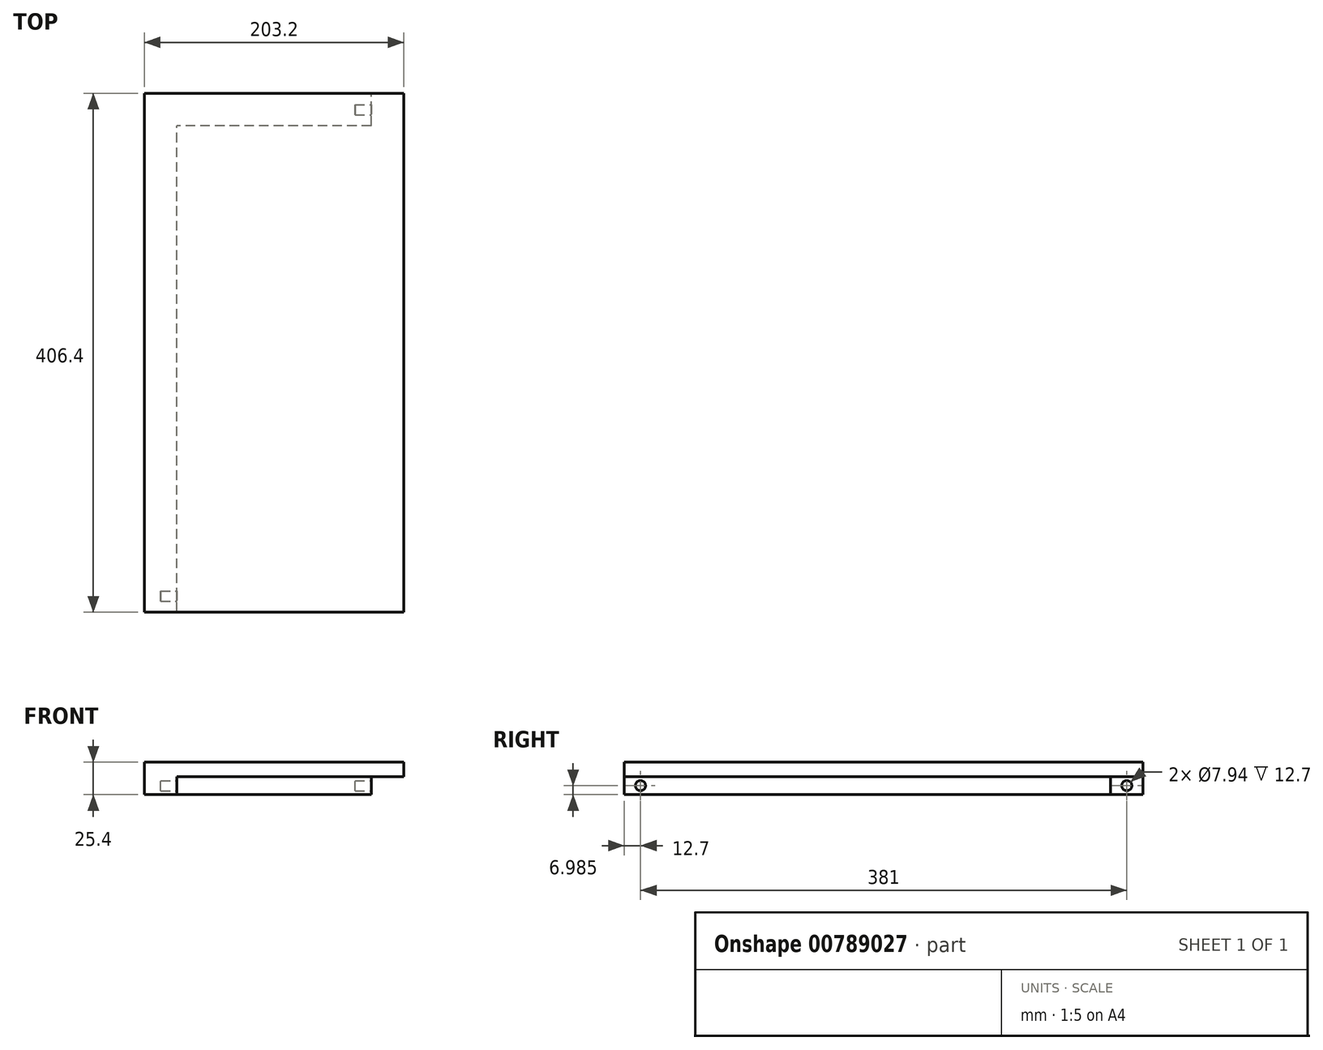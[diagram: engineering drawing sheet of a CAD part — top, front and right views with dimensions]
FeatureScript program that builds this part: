
annotation { "Feature Type Name" : "Feature", "Feature Type Description" : "" }
export const myFeature = defineFeature(function(context is Context, id is Id, definition is map)
    precondition{}
    {
        {
            var Q0;
            Q0=qCreatedBy(makeId("Top.planeOp"),FACE);
            var sketch = newSketch(context, id + "F0", { "sketchPlane" : qUnion([Q0])});
            skLineSegment(sketch, "E0.bottom", {"start": v(101.6, 203.2) * mm, "end": v(-101.6, 203.2) * mm});
            skLineSegment(sketch, "E0.top", {"start": v(101.6, -203.2) * mm, "end": v(-101.6, -203.2) * mm});
            skLineSegment(sketch, "E0.left", {"start": v(101.6, 203.2) * mm, "end": v(101.6, -203.2) * mm});
            skLineSegment(sketch, "E0.right", {"start": v(-101.6, 203.2) * mm, "end": v(-101.6, -203.2) * mm});
            skPoint(sketch, "E0.middle", {"position": v(0, 0) * mm});
            skLineSegment(sketch, "E1", {"start": v(-101.6, 177.8) * mm, "end": v(101.6, 177.8) * mm});
            skLineSegment(sketch, "E2", {"start": v(-76.2, 203.2) * mm, "end": v(-76.2, -203.2) * mm});
            skLineSegment(sketch, "E3", {"start": v(76.2, 203.2) * mm, "end": v(76.2, 177.8) * mm});
            skSolve(sketch);
        }
        {
            var Q0;
            {var subQ0=sQuery(id+"F0.wireOp",EDGE,"E0.right");var subQ1=sQuery(id+"F0.wireOp",EDGE,"E0.bottom");var subQ2=makeQuery(id+"F0.imprint","INTERSECT",VERTEX,{"derivedFrom":[subQ1,subQ0]});Q0=makeQuery(id+"F0.imprint","IMPRINT",FACE,{"disambiguationData":[TD([[makeQuery(id+"F0.imprint","IMPRINT",EDGE,{"disambiguationData":[TD([[subQ2,1.0]])],"derivedFrom":subQ1}),1.0]])]});}
            var Q1;
            {var subQ0=sQuery(id+"F0.wireOp",EDGE,"E0.right");var subQ1=sQuery(id+"F0.wireOp",EDGE,"E0.top");var subQ2=makeQuery(id+"F0.imprint","INTERSECT",VERTEX,{"derivedFrom":[subQ1,subQ0]});Q1=makeQuery(id+"F0.imprint","IMPRINT",FACE,{"disambiguationData":[TD([[makeQuery(id+"F0.imprint","IMPRINT",EDGE,{"disambiguationData":[TD([[subQ2,1.0]])],"derivedFrom":subQ1}),-1.0]])]});}
            var Q2;
            {var subQ3=sQuery(id+"F0.wireOp",EDGE,"E3");Q2=makeQuery(id+"F0.imprint","IMPRINT",FACE,{"disambiguationData":[TD([[makeQuery(id+"F0.imprint","IMPRINT",EDGE,{"derivedFrom":subQ3}),-1.0]])]});}
            extrude(context, id + "F1", {"entities" : qUnion([Q0, Q1, Q2]), "oppositeDirection" : true, "depth" : 25.4 * mm, "offsetDistance" : 25.4 * mm});
        }
        {
            var Q0;
            {var subQ0=sQuery(id+"F0.wireOp",EDGE,"E0.right");var subQ1=sQuery(id+"F0.wireOp",EDGE,"E0.bottom");var subQ2=makeQuery(id+"F0.imprint","INTERSECT",VERTEX,{"derivedFrom":[subQ1,subQ0]});Q0=makeQuery(id+"F0.imprint","IMPRINT",FACE,{"disambiguationData":[TD([[makeQuery(id+"F0.imprint","IMPRINT",EDGE,{"disambiguationData":[TD([[subQ2,1.0]])],"derivedFrom":subQ1}),1.0]])]});}
            var Q1;
            {var subQ0=sQuery(id+"F0.wireOp",EDGE,"E0.right");var subQ1=sQuery(id+"F0.wireOp",EDGE,"E0.top");var subQ2=makeQuery(id+"F0.imprint","INTERSECT",VERTEX,{"derivedFrom":[subQ1,subQ0]});Q1=makeQuery(id+"F0.imprint","IMPRINT",FACE,{"disambiguationData":[TD([[makeQuery(id+"F0.imprint","IMPRINT",EDGE,{"disambiguationData":[TD([[subQ2,1.0]])],"derivedFrom":subQ1}),-1.0]])]});}
            var Q2;
            {var subQ3=sQuery(id+"F0.wireOp",EDGE,"E3");Q2=makeQuery(id+"F0.imprint","IMPRINT",FACE,{"disambiguationData":[TD([[makeQuery(id+"F0.imprint","IMPRINT",EDGE,{"derivedFrom":subQ3}),-1.0]])]});}
            var Q3;
            {var subQ4=sQuery(id+"F0.wireOp",EDGE,"E0.left");var subQ6=sQuery(id+"F0.wireOp",EDGE,"E0.top");var subQ7=makeQuery(id+"F0.imprint","INTERSECT",VERTEX,{"derivedFrom":[subQ6,subQ4]});Q3=makeQuery(id+"F0.imprint","IMPRINT",FACE,{"disambiguationData":[TD([[makeQuery(id+"F0.imprint","IMPRINT",EDGE,{"disambiguationData":[TD([[subQ7,-1.0]])],"derivedFrom":subQ6}),-1.0]])]});}
            var Q4;
            {var subQ3=sQuery(id+"F0.wireOp",EDGE,"E3");Q4=makeQuery(id+"F0.imprint","IMPRINT",FACE,{"disambiguationData":[TD([[makeQuery(id+"F0.imprint","IMPRINT",EDGE,{"derivedFrom":subQ3}),1.0]])]});}
            extrude(context, id + "F2", {"entities" : qUnion([Q0, Q1, Q2, Q3, Q4]), "operationType" : NewBodyOperationType.ADD, "oppositeDirection" : true, "depth" : 11.43 * mm, "offsetDistance" : 25.4 * mm});
        }
        {
            var Q0;
            Q0=makeQuery(id+"F1.opExtrude","SWEPT_FACE",FACE,{"disambiguationData":[OSD([sQuery(id+"F0.wireOp",EDGE,"E2")])]});
            var sketch = newSketch(context, id + "F3", { "sketchPlane" : qUnion([Q0])});
            skCircle(sketch, "E4", {"center": v(-190.5, -18.41) * mm, "radius": 3.97 * mm});
            skSolve(sketch);
        }
        {
            var Q0;
            Q0=makeQuery(id+"F1.opExtrude","SWEPT_FACE",FACE,{"disambiguationData":[OSD([sQuery(id+"F0.wireOp",EDGE,"E3")])]});
            var sketch = newSketch(context, id + "F4", { "sketchPlane" : qUnion([Q0])});
            skCircle(sketch, "E5", {"center": v(190.5, -18.41) * mm, "radius": 3.97 * mm});
            skPoint(sketch, "E5.centerSnap0", {"position": v(190.5, -11.43) * mm});
            skSolve(sketch);
        }
        {
            var Q0;
            Q0 = qSketchRegion(id + "F4", true);
            extrude(context, id + "F5", {"entities" : qUnion([Q0]), "operationType" : NewBodyOperationType.REMOVE, "oppositeDirection" : true, "depth" : 12.7 * mm, "offsetDistance" : 25.4 * mm});
        }
        {
            var Q0;
            Q0=makeQuery(id+"F3.imprint","IMPRINT",FACE,{"disambiguationData":[TD([[makeQuery(id+"F3.imprint","IMPRINT",EDGE,{"derivedFrom":sQuery(id+"F3.wireOp",EDGE,"E4")}),1.0]])]});
            extrude(context, id + "F6", {"entities" : qUnion([Q0]), "operationType" : NewBodyOperationType.REMOVE, "oppositeDirection" : true, "depth" : 12.7 * mm, "offsetDistance" : 25.4 * mm});
        }
    });
